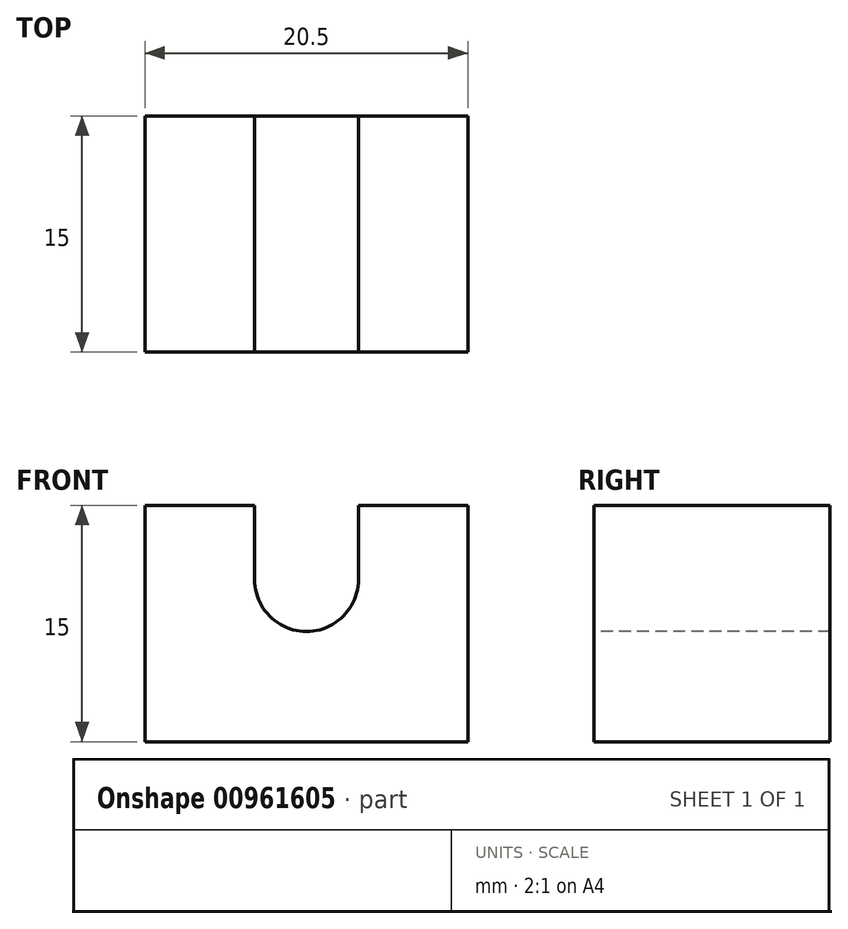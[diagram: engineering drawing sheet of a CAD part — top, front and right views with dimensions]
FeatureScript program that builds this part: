
annotation { "Feature Type Name" : "Feature", "Feature Type Description" : "" }
export const myFeature = defineFeature(function(context is Context, id is Id, definition is map)
    precondition{}
    {
        {
            var Q0;
            Q0=qCreatedBy(makeId("Front.planeOp"),FACE);
            var sketch = newSketch(context, id + "F0", { "sketchPlane" : qUnion([Q0])});
            skLineSegment(sketch, "E0.bottom", {"start": v(0, 0) * mm, "end": v(20.5, 0) * mm});
            skLineSegment(sketch, "E0.top", {"start": v(0, 15) * mm, "end": v(20.5, 15) * mm});
            skLineSegment(sketch, "E0.left", {"start": v(0, 0) * mm, "end": v(0, 15) * mm});
            skLineSegment(sketch, "E0.right", {"start": v(20.5, 0) * mm, "end": v(20.5, 15) * mm});
            skSolve(sketch);
        }
        {
            var Q0;
            Q0 = qSketchRegion(id + "F0", true);
            extrude(context, id + "F1", {"entities" : qUnion([Q0]), "depth" : 15 * mm, "offsetDistance" : 25 * mm});
        }
        {
            var Q0;
            Q0=makeQuery(id+"F1.opExtrude","CAP_FACE",FACE,{"disambiguationData":[OSD([sQuery(id+"F0.wireOp",EDGE,"E0.bottom"),sQuery(id+"F0.wireOp",EDGE,"E0.top"),sQuery(id+"F0.wireOp",EDGE,"E0.left"),sQuery(id+"F0.wireOp",EDGE,"E0.right")])],"isStart":false});
            var sketch = newSketch(context, id + "F2", { "sketchPlane" : qUnion([Q0])});
            skCircle(sketch, "E1", {"center": v(10.25, 10.3) * mm, "radius": 3.3 * mm});
            skPoint(sketch, "E1.centerSnap0", {"position": v(10.25, 15) * mm});
            skLineSegment(sketch, "E2", {"start": v(6.95, 10.3) * mm, "end": v(6.95, 15) * mm});
            skLineSegment(sketch, "E3", {"start": v(13.55, 10.3) * mm, "end": v(13.55, 15) * mm});
            skLineSegment(sketch, "E4", {"start": v(13.55, 15) * mm, "end": v(6.95, 15) * mm});
            skSolve(sketch);
        }
        {
            var Q0;
            Q0 = qSketchRegion(id + "F2", true);
            extrude(context, id + "F3", {"entities" : qUnion([Q0]), "operationType" : NewBodyOperationType.REMOVE, "endBound" : BoundingType.THROUGH_ALL, "oppositeDirection" : true, "depth" : 7 * mm, "offsetDistance" : 25 * mm});
        }
    });
